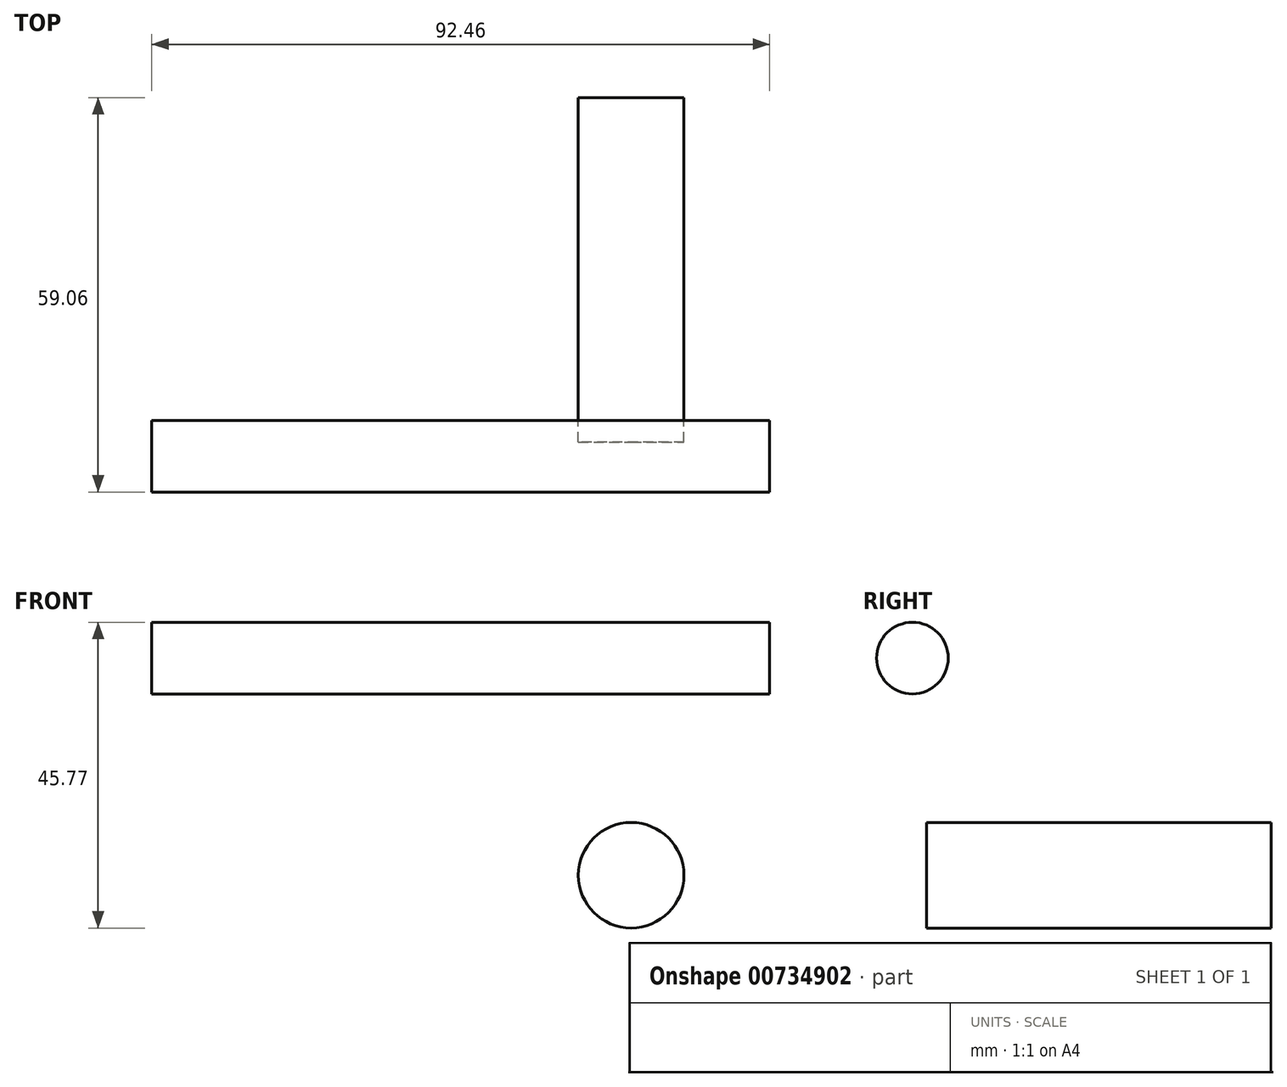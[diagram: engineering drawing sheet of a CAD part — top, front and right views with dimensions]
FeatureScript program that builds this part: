
annotation { "Feature Type Name" : "Feature", "Feature Type Description" : "" }
export const myFeature = defineFeature(function(context is Context, id is Id, definition is map)
    precondition{}
    {
        {
            var Q0;
            Q0=qCreatedBy(makeId("Right.planeOp"),FACE);
            var sketch = newSketch(context, id + "F0", { "sketchPlane" : qUnion([Q0])});
            skCircle(sketch, "E0", {"center": v(-53.7, 63.55) * mm, "radius": 5.36 * mm});
            skSolve(sketch);
        }
        {
            var Q0;
            Q0 = qSketchRegion(id + "F0", true);
            var Q1;
            Q1=makeQuery(id+"F0.imprint","IMPRINT",FACE,{"disambiguationData":[TD([[makeQuery(id+"F0.imprint","IMPRINT",EDGE,{"derivedFrom":sQuery(id+"F0.wireOp",EDGE,"E0")}),1.0]])]});
            extrude(context, id + "F1", {"entities" : qUnion([Q0, Q1]), "depth" : 92.46 * mm, "offsetDistance" : 25.4 * mm});
        }
        {
            var Q0;
            Q0=qCreatedBy(makeId("Front.planeOp"),FACE);
            var sketch = newSketch(context, id + "F2", { "sketchPlane" : qUnion([Q0])});
            skCircle(sketch, "E1", {"center": v(71.74, 31.04) * mm, "radius": 7.9 * mm});
            skSolve(sketch);
        }
        {
            var Q0;
            Q0 = qSketchRegion(id + "F2", true);
            var Q1;
            Q1=makeQuery(id+"F2.imprint","IMPRINT",FACE,{"disambiguationData":[TD([[makeQuery(id+"F2.imprint","IMPRINT",EDGE,{"derivedFrom":sQuery(id+"F2.wireOp",EDGE,"E1")}),1.0]])]});
            extrude(context, id + "F3", {"entities" : qUnion([Q0, Q1]), "depth" : 51.56 * mm, "offsetDistance" : 25.4 * mm});
        }
    });
